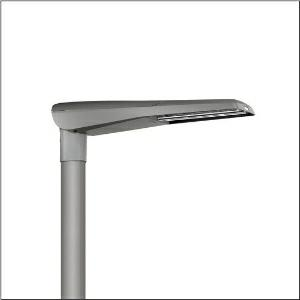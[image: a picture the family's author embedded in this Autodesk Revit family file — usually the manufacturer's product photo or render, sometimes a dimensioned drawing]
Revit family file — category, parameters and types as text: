
# Revit family: streetlight_sl_11_iq_mini___st0_5a_5xc2bc1f08he_0989
name_source: partatom
category: Lighting Fixtures
units: mm (PartAtom-declared; Revit-internal decimal feet)

## family parameters
Cut with Voids When Loaded = No
Host = Face
Light Source = No
Part Type = Normal
Room Calculation Point = No
Round Connector Dimension = Use Diameter
Shared = No

## types (1)
- --- (1 x LED, 6780 lm, 63.6 W, 2200K)
    Apparent Load = 64 VA
    CIE Flux Codes = 43 74 97 100 100
    Color Rendering = 70
    Color Temperature = 2200K
    Default Elevation = 1800 mm
    Description = Streetlight SL 11 iQ mini, mast luminaire, primary light control with 3 zone facetted reflector, of plastic, silver coated, highly specular, primary optical cover: cover, of PMMA, transparent, light distribution: ST0.5a, light emission: direct distribution, primary light characteristic: asymmetric, installation type: post-top, side-entry, lamps: LED, High Power LED, rated values: 8.280lm | 62,2W | 133,1lm/W (begin service life); end service life: 8.280lm | 65,6W; at 50% lumin. flux: 4.140lm | 29,4W | 140,8lm/W, colour temperature: 2200/2700/3000/4000K, colour rendering: CRI > 70, light colour: 722/727/730/740, light setting 1 begin service life: 100% | 8.280lm | 62,2W | 133,1lm/W | 3.000K, light setting 1 end service life: 65,6W, further light settings possible, control: Street-Remote, Auto-Match, Temp-Guard, Lumen-Switch, Night-Set, Smart-Wire, Light-Fading, Desk-Remote (wireless, voltage-free reading and setting of iQ features in the workshop via application-optimized NFC function/RFID function), optimised constant luminous flux control (CLO 2.0), with cable H07RN-F 3x 1.5mm², mains connection: 230..240V, AC, 50/60Hz, connection cable pre-assembled, cable length: 8,5m, luminaire housing, of diecast aluminium, powder-coated, SITECO metallic grey (DB 702S), please order mast flange separately, inclination adjustable without tools: 0°, 5°, 10°, 15° (post-top) | 0°, -5°, -10°, -15° (side-entry), sealing non-destructively replaceable, multi-level sealing system, length: 736mm, width: 174mm, height: 116mm, mast flange for spigot size: 42mm (side-entry): 5XC10008XM4, 60/48mm (side-entry/post-top): 5XC10108XM2, 76/60mm (side-entry/post-top): 5XC10108XM1, equipment: Power, protection rating (complete): IP66, insulation class (complete): insulation class II (safety insulation), certification: CE, ENEC, ENEC+, VDE, impact resistance: IK10, permissible operating ambient temperature for outdoor applications: -25..+50°C, standard-compliant lighting for roads and squares, Environmental Product Declaration (EPD) tested and certified by an independent institute, packaging unit: 1 piece

Light Distribution: ST0.5a
    Height = 116 mm
    Lamp = 1 x LED
    Lamp Light Flux = 6780 lm
    Lamp Power = 63.6 W
    Lamp count = 1
    Length = 736 mm
    Luminous efficacy = 107 lm/W
    Manufacturer = Siteco
    ModVariant = No
    Model = 5XC2BC1F08HE
    Number of Poles = 1
    OnlyDefault = Yes
    Power Factor = 1
    Product Name = Streetlight SL 11 iQ mini | ST0.5a
    Product group = mast luminaire | pylon top
    ProductGroupID = 6100
    Protection Class = Protection class II
    Protection Degree = IP 66
    RLX_Detail_Level = 1
    RLX_Emergency_Light_Flux = 0 lm
    RLX_Emergency_Type = 0
    RLX_Emergency_Type_DB = No
    RlxData = <blob elided: 58377 chars, md5=ec75d38b>
    Socket = socket
    Standby Power = 0 W
    System Light Flux = 6780 lm
    System Power = 64 W
    Type Comments = individual setting: luminous flux: 100 % | dim-lin: 254 | 866 mA
    Type Image = l_1003508.jpg
    URL = http://relux.com
    VarID = @adj_042767
    Voltage = 0 V
    Weight = 0.00 kg
    Width = 174 mm

## geometry (parser evidence)
native form markers: Blend x4, Sweep x11
no freeform markers — native parametric forms only
